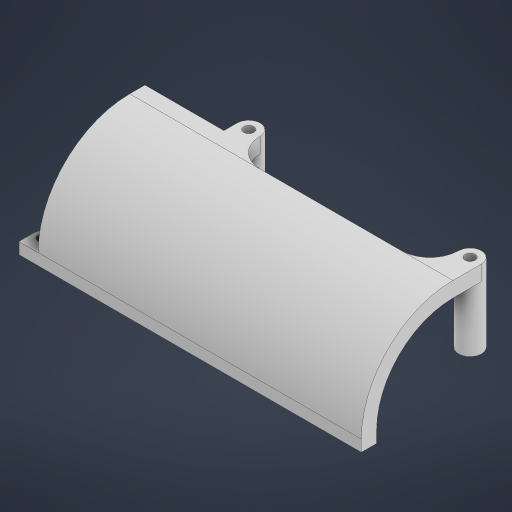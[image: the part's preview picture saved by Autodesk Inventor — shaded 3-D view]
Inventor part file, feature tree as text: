
AUTODESK INVENTOR PART (.ipt)
format: ipt  version: 2024.1 (Build 281209000, 209)  size: 667,136 bytes
history: native  units: mm
features: extrude x14, sketch x12, projected_geometry x8, fillet x4, chamfer x2, other x1
ambient origin geometry x8: Origin, YZ Plane, XZ Plane, XY Plane, X Axis, Y Axis, Z Axis, Center Point
bodies: Body1 (feature_tree)
feature tree (41):
  other  "솔리드1"
  extrude  "돌출1"  Depth=3.0mm
  extrude  "돌출2"  Depth=5.0mm
  extrude  "돌출3"  Depth=4.0mm
  extrude  "돌출4"  Depth=85.0mm
  sketch  "스케치5"
  extrude  "돌출5"  Depth=5.0mm
  fillet  "모깎기1"  [1 undecoded]
  fillet  "모깎기2"  Radius=3.0mm
  extrude  "돌출6"  Depth=20.0mm
  extrude  "돌출7"  Depth=80.0mm TaperAngle=0.0deg
  sketch  "스케치7"
  extrude  "돌출8"  Depth=4.7mm TaperAngle=0.0deg
  extrude  "돌출9"  Depth=6.0mm
  fillet  "모깎기4"  Radius=4.0mm
  fillet  "모깎기6"  Radius=10.5mm
  extrude  "돌출10"  Depth=2.7mm
  extrude  "돌출11"  Depth=6.0mm
  extrude  "돌출12"  Depth=16.42mm TaperAngle=0.0deg
  extrude  "돌출14"  Depth=3.0mm
  chamfer  "모따기2"  Distance=7.5mm
  chamfer  "모따기3"  Distance=16.42mm
  extrude  "돌출15"  Depth=6.0mm
  sketch  "스케치1"
  sketch  "스케치2"
  projected_geometry  "투영된 루프1"
  sketch  "스케치3"
  projected_geometry  "투영된 루프2"
  sketch  "스케치4"
  projected_geometry  "투영된 루프3"
  sketch  "스케치6"
  sketch  "스케치8"
  projected_geometry  "투영된 루프4"
  sketch  "스케치9"
  projected_geometry  "투영된 루프5"
  sketch  "스케치10"
  projected_geometry  "투영된 루프6"
  projected_geometry  "투영된 루프8"
  sketch  "스케치13"
  projected_geometry  "투영된 루프10"
  sketch  "스케치14"
note: 1 required parameter value undecoded (feature->parameter linkage not recoverable at this tier; creation-order binding heuristic only, values carry confidence <= 0.55)
